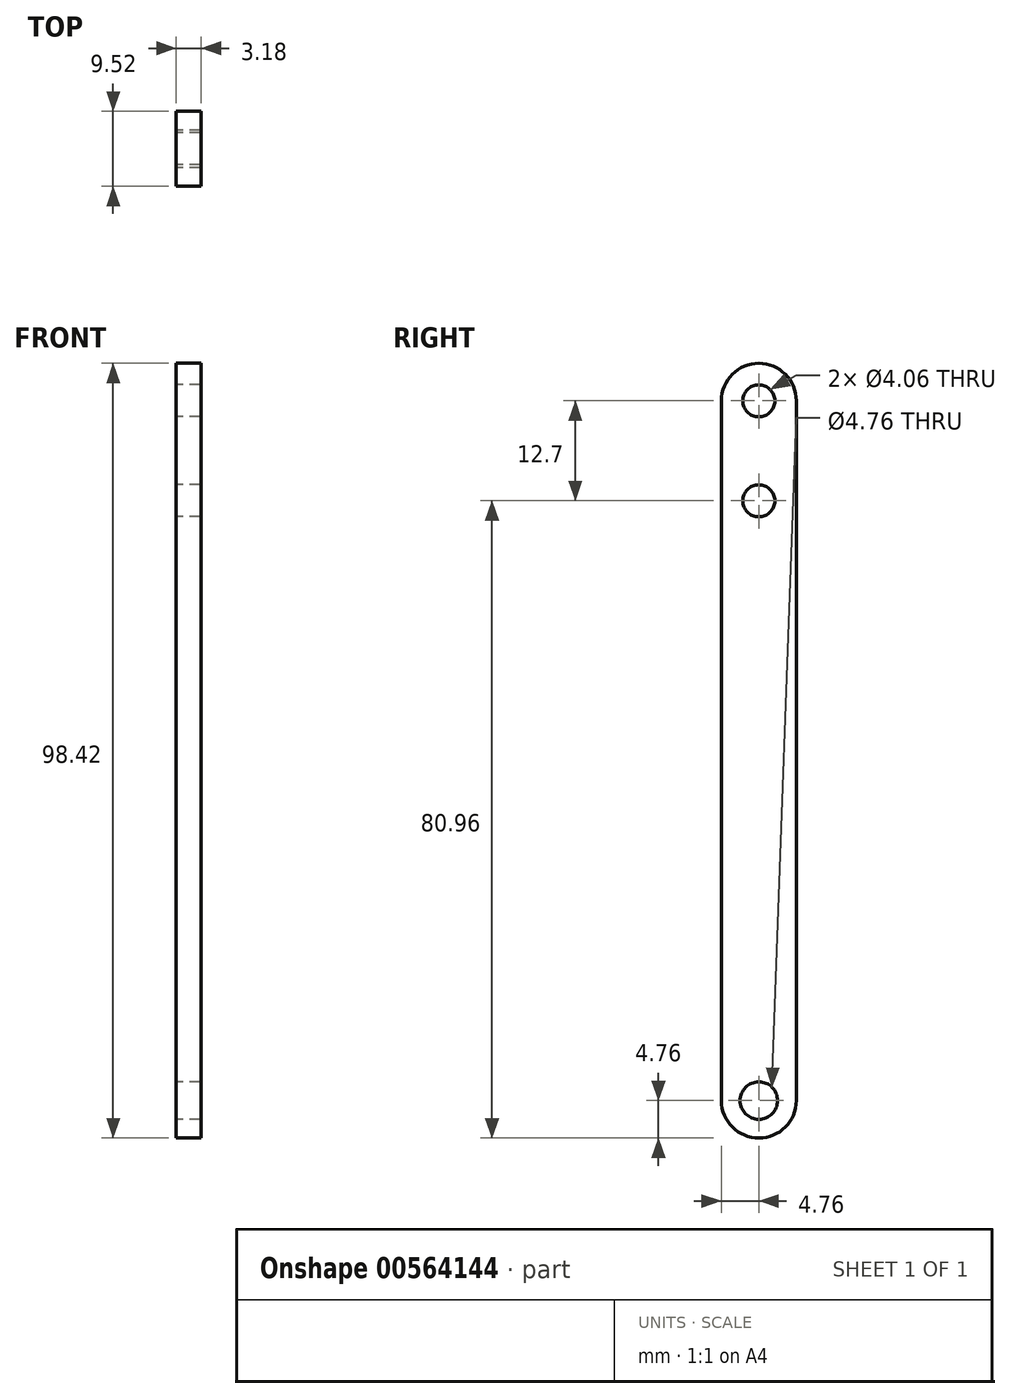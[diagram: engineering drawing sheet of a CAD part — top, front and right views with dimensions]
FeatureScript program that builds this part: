
annotation { "Feature Type Name" : "Feature", "Feature Type Description" : "" }
export const myFeature = defineFeature(function(context is Context, id is Id, definition is map)
    precondition{}
    {
        {
            var Q0;
            Q0=qCreatedBy(makeId("Right.planeOp"),FACE);
            var sketch = newSketch(context, id + "F0", { "sketchPlane" : qUnion([Q0])});
            skCircle(sketch, "E0", {"center": v(0, 0) * mm, "radius": 2.38 * mm});
            skCircle(sketch, "E1", {"center": v(0, 88.9) * mm, "radius": 2.03 * mm});
            skArc(sketch, "E2", {"start": v(4.76, 88.9) * mm, "mid": v(0, 93.66) * mm, "end": v(-4.76, 88.9) * mm});
            skCircle(sketch, "E3", {"center": v(0, 0) * mm, "radius": 4.76 * mm});
            skLineSegment(sketch, "E4", {"start": v(-4.76, 88.9) * mm, "end": v(-4.76, 0) * mm});
            skLineSegment(sketch, "E5", {"start": v(4.76, 88.9) * mm, "end": v(4.76, 0) * mm});
            skCircle(sketch, "E6", {"center": v(0, 76.2) * mm, "radius": 2.03 * mm});
            skSolve(sketch);
        }
        {
            var Q0;
            Q0=qSketchRegion(id+"F0",true);
            extrude(context, id + "F1", {"entities" : qUnion([Q0]), "depth" : 3.17 * mm, "offsetDistance" : 25.4 * mm});
        }
    });
